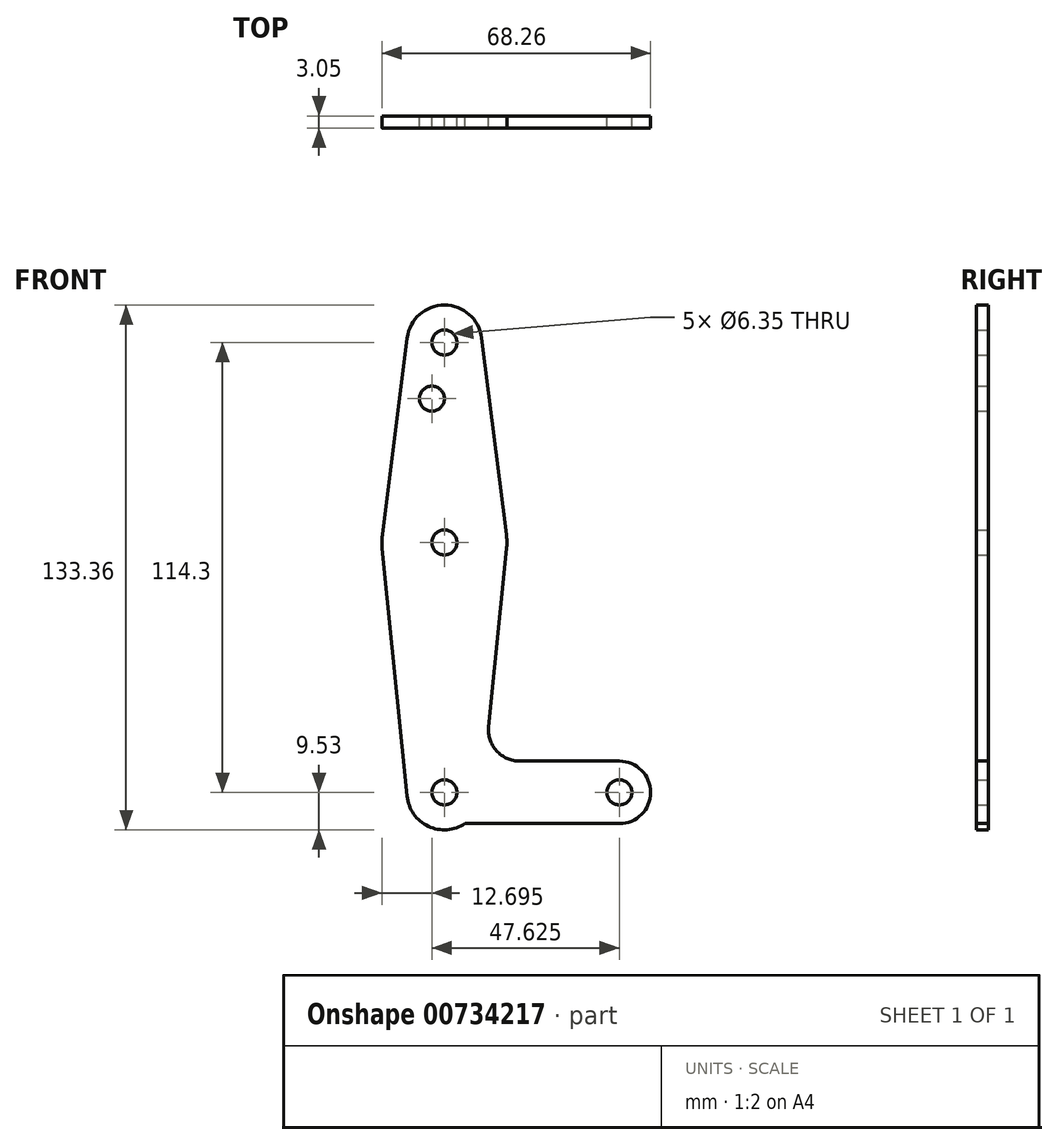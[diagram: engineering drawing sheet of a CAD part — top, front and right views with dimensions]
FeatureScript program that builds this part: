
annotation { "Feature Type Name" : "Feature", "Feature Type Description" : "" }
export const myFeature = defineFeature(function(context is Context, id is Id, definition is map)
    precondition{}
    {
        {
            var Q0;
            Q0=qCreatedBy(makeId("Front.planeOp"),FACE);
            var sketch = newSketch(context, id + "F0", { "sketchPlane" : qUnion([Q0])});
            skLineSegment(sketch, "E0", {"start": v(0, 0) * mm, "end": v(0, 114.3) * mm, "construction": true});
            skCircle(sketch, "E1", {"center": v(0, 0) * mm, "radius": 9.53 * mm});
            skCircle(sketch, "E2", {"center": v(0, 63.5) * mm, "radius": 15.88 * mm});
            skLineSegment(sketch, "E3", {"start": v(0, 0) * mm, "end": v(44.45, 0) * mm, "construction": true});
            skCircle(sketch, "E4", {"center": v(44.45, 0) * mm, "radius": 7.94 * mm});
            skPoint(sketch, "E5.center.orphan", {"position": v(0, 127) * mm});
            skCircle(sketch, "E6", {"center": v(0, 114.3) * mm, "radius": 9.53 * mm});
            skLineSegment(sketch, "E7", {"start": v(-9.45, 115.5) * mm, "end": v(-15.75, 65.48) * mm});
            skLineSegment(sketch, "E8", {"start": v(9.45, 115.5) * mm, "end": v(15.75, 65.48) * mm});
            skLineSegment(sketch, "E9", {"start": v(-15.8, 61.91) * mm, "end": v(-9.48, -0.95) * mm});
            skLineSegment(sketch, "E10", {"start": v(15.8, 61.91) * mm, "end": v(11.25, 16.68) * mm});
            skLineSegment(sketch, "E11", {"start": v(5.27, -7.94) * mm, "end": v(44.45, -7.94) * mm});
            skLineSegment(sketch, "E12", {"start": v(19.16, 7.94) * mm, "end": v(44.45, 7.94) * mm});
            skCircle(sketch, "E13", {"center": v(0, 114.3) * mm, "radius": 3.18 * mm});
            skCircle(sketch, "E14", {"center": v(0, 63.5) * mm, "radius": 3.18 * mm});
            skCircle(sketch, "E15", {"center": v(0, 0) * mm, "radius": 3.18 * mm});
            skCircle(sketch, "E16", {"center": v(44.45, 0) * mm, "radius": 3.18 * mm});
            skCircle(sketch, "E17", {"center": v(-3.18, 100.03) * mm, "radius": 3.18 * mm});
            skArc(sketch, "E18.filletArc", {"start": v(11.25, 16.68) * mm, "mid": v(13.26, 10.55) * mm, "end": v(19.16, 7.94) * mm});
            skSolve(sketch);
        }
        {
            var Q0;
            Q0 = qSketchRegion(id + "F0", true);
            extrude(context, id + "F1", {"entities" : qUnion([Q0]), "depth" : 3.05 * mm, "offsetDistance" : 25.4 * mm});
        }
    });
